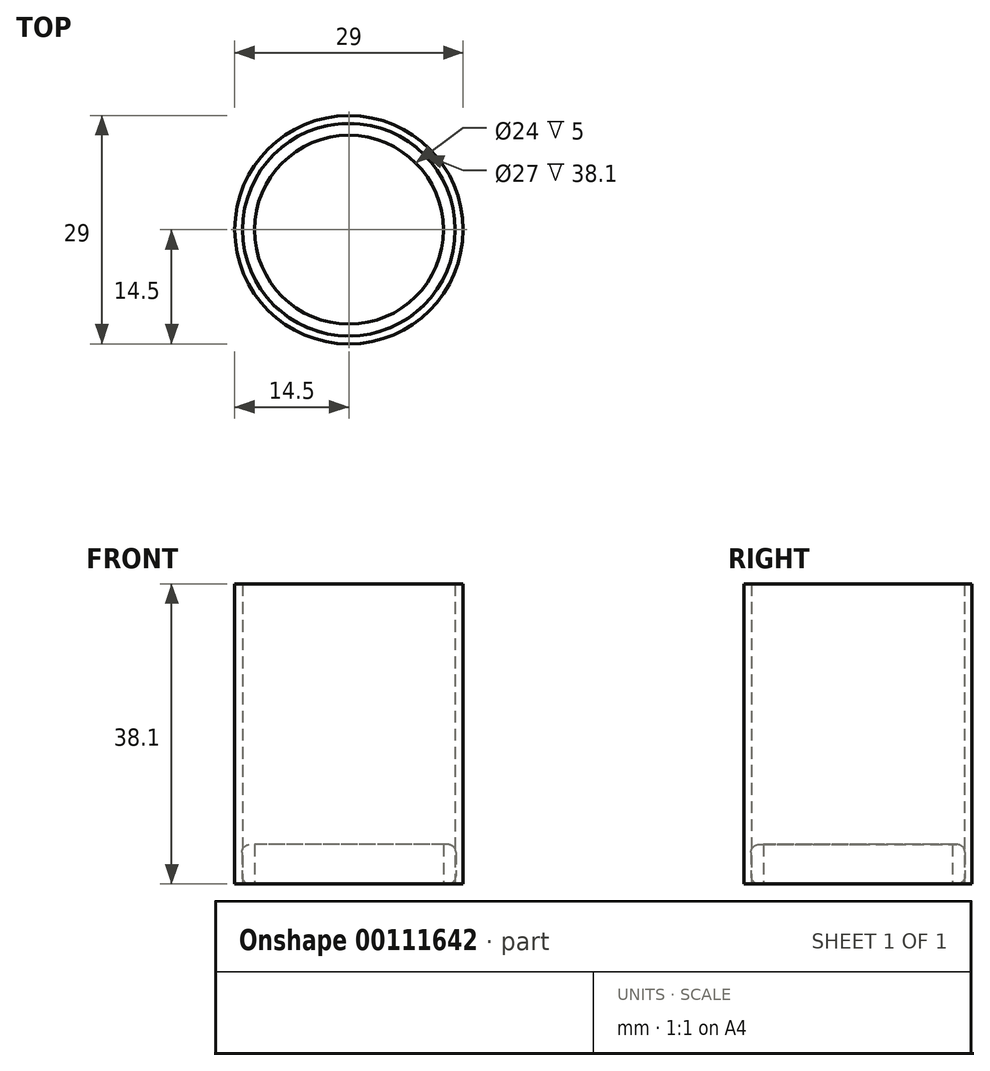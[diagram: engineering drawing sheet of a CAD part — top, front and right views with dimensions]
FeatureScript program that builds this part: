
annotation { "Feature Type Name" : "Feature", "Feature Type Description" : "" }
export const myFeature = defineFeature(function(context is Context, id is Id, definition is map)
    precondition{}
    {
        {
            var Q0;
            Q0=qCreatedBy(makeId("Top.planeOp"),FACE);
            var sketch = newSketch(context, id + "F0", { "sketchPlane" : qUnion([Q0])});
            skCircle(sketch, "E0", {"center": v(0, 0) * mm, "radius": 62.03 * mm});
            skCircle(sketch, "E1", {"center": v(0, 0) * mm, "radius": 57.77 * mm});
            skLineSegment(sketch, "E2", {"start": v(0, -57.77) * mm, "end": v(0, -62.03) * mm});
            skSolve(sketch);
        }
        {
            var Q0;
            Q0=qCreatedBy(makeId("Top.planeOp"),FACE);
            cPlane(context, id + "F1", {"entities" : qUnion([Q0]), "cplaneType" : CPlaneType.OFFSET, "offset" : 76.2 * mm, "width" : 152.4 * mm, "height" : 152.4 * mm});
        }
        {
            var Q0;
            Q0=qCreatedBy(id+"F1.planeOp",FACE);
            var sketch = newSketch(context, id + "F2", { "sketchPlane" : qUnion([Q0])});
            skCircle(sketch, "E3", {"center": v(0, 0) * mm, "radius": 13.5 * mm});
            skCircle(sketch, "E4", {"center": v(0, 0) * mm, "radius": 14.5 * mm});
            skSolve(sketch);
        }
        {
            var Q0;
            Q0=qCreatedBy(makeId("Front.planeOp"),FACE);
            var sketch = newSketch(context, id + "F3", { "sketchPlane" : qUnion([Q0])});
            skLineSegment(sketch, "E5", {"start": v(12.74, 77.12) * mm, "end": v(56.93, 0) * mm});
            skSolve(sketch);
        }
        {
            var Q0;
            Q0=sQuery(id+"F3.wireOp",EDGE,"E5");
            var Q1;
            Q1=sQuery(id+"F2.wireOp",EDGE,"E3");
            revolve(context, id + "F4", {"bodyType" : ToolBodyType.SURFACE, "surfaceEntities" : qUnion([Q0]), "axis" : qUnion([Q1]), "revolveType" : RevolveType.FULL});
        }
        {
            var Q0;
            Q0=qCreatedBy(makeId("Front.planeOp"),FACE);
            var sketch = newSketch(context, id + "F5", { "sketchPlane" : qUnion([Q0])});
            skLineSegment(sketch, "E6", {"start": v(-62.28, 0) * mm, "end": v(-15.75, 75.4) * mm});
            skSolve(sketch);
        }
        {
            var Q0;
            Q0=sQuery(id+"F5.wireOp",EDGE,"E6");
            var Q1;
            Q1=sQuery(id+"F2.wireOp",EDGE,"E4");
            revolve(context, id + "F6", {"bodyType" : ToolBodyType.SURFACE, "surfaceEntities" : qUnion([Q0]), "axis" : qUnion([Q1]), "revolveType" : RevolveType.FULL});
        }
        {
            var Q0;
            Q0=sQuery(id+"F0.wireOp",EDGE,"E2");
            var Q1;
            Q1=sQuery(id+"F0.wireOp",EDGE,"E1");
            revolve(context, id + "F7", {"bodyType" : ToolBodyType.SURFACE, "surfaceEntities" : qUnion([Q0]), "axis" : qUnion([Q1]), "revolveType" : RevolveType.FULL});
        }
        {
            var Q0;
            Q0=makeQuery(id+"F2.imprint","IMPRINT",FACE,{"disambiguationData":[TD([[makeQuery(id+"F2.imprint","IMPRINT",EDGE,{"derivedFrom":sQuery(id+"F2.wireOp",EDGE,"E3")}),-1.0]])]});
            extrude(context, id + "F8", {"entities" : qUnion([Q0]), "depth" : 38.1 * mm});
        }
        {
            var Q0;
            Q0=makeQuery(id+"F8.opExtrude","CAP_FACE",FACE,{"disambiguationData":[OSD([sQuery(id+"F2.wireOp",EDGE,"E3"),sQuery(id+"F2.wireOp",EDGE,"E4")])],"isStart":false});
            var sketch = newSketch(context, id + "F9", { "sketchPlane" : qUnion([Q0])});
            skCircle(sketch, "E7", {"center": v(0, 0) * mm, "radius": 13 * mm});
            skSolve(sketch);
        }
        {
            var Q0;
            Q0=qCreatedBy(id+"F1.planeOp",FACE);
            var sketch = newSketch(context, id + "F10", { "sketchPlane" : qUnion([Q0])});
            skCircle(sketch, "E8", {"center": v(0, 0) * mm, "radius": 13.6 * mm});
            skCircle(sketch, "E9", {"center": v(0, 0) * mm, "radius": 12 * mm});
            skSolve(sketch);
        }
        {
            var Q0;
            Q0 = qSketchRegion(id + "F10", true);
            extrude(context, id + "F11", {"entities" : qUnion([Q0]), "depth" : 5 * mm});
        }
        {
            var Q0;
            Q0=makeQuery(id+"F11.opExtrude","CAP_EDGE",EDGE,{"disambiguationData":[OSD([sQuery(id+"F10.wireOp",EDGE,"E8")])],"isStart":true});
            var Q1;
            Q1=makeQuery(id+"F11.opExtrude","CAP_EDGE",EDGE,{"disambiguationData":[OSD([sQuery(id+"F10.wireOp",EDGE,"E8")])],"isStart":false});
            fillet(context, id + "F12", {"entities" : qUnion([Q0, Q1]), "radius" : 1 * mm, "tangentPropagation" : true, "allowEdgeOverflow" : false});
        }
    });
